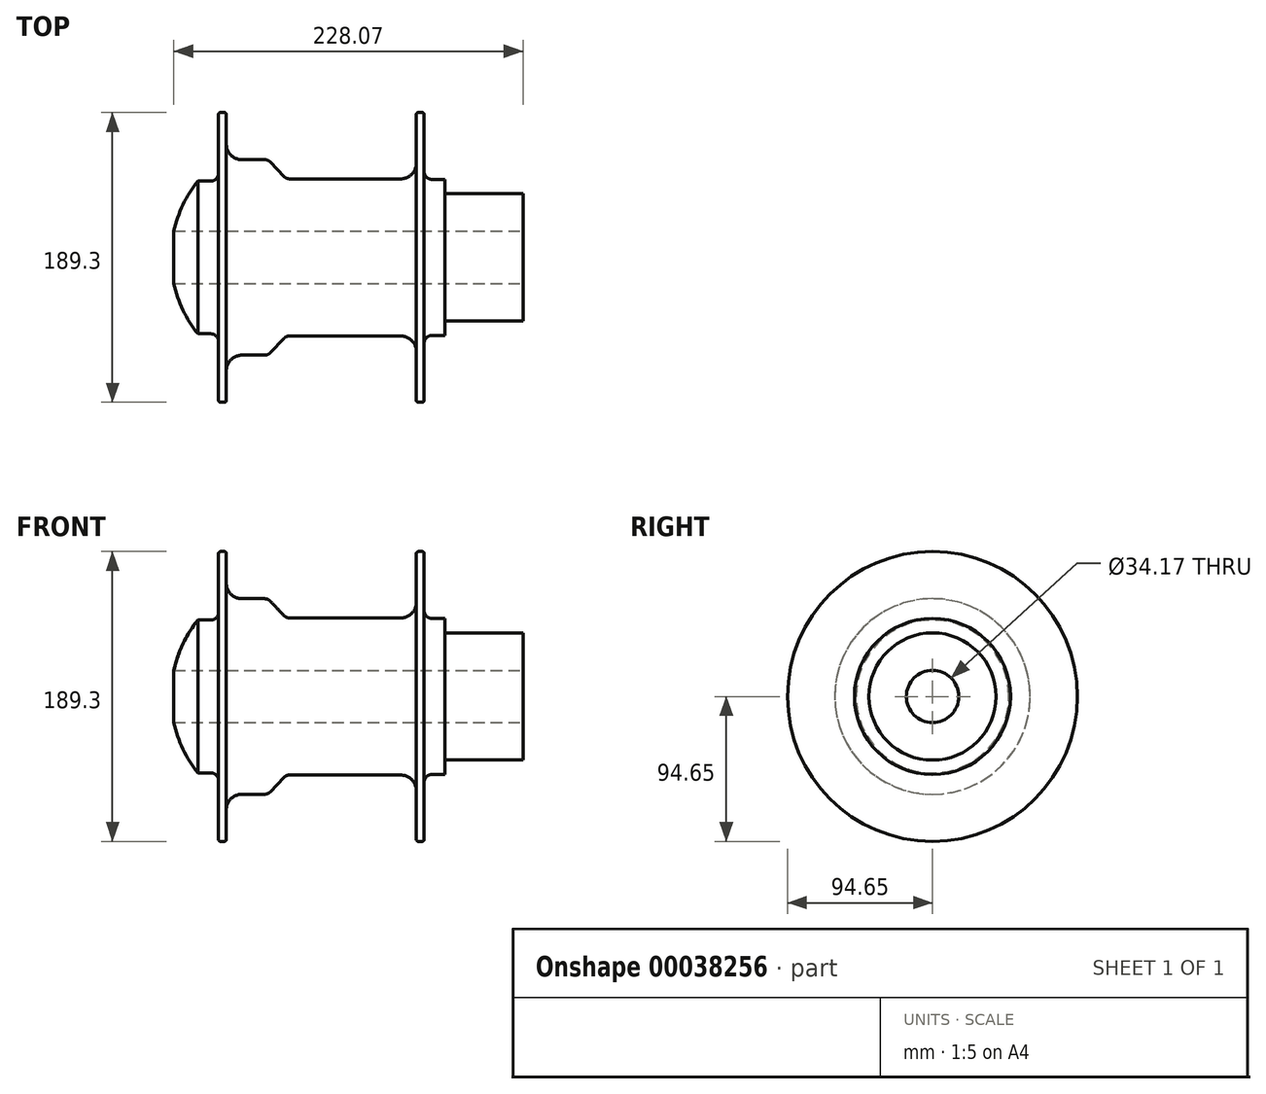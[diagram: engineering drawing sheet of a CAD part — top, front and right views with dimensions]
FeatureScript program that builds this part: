
annotation { "Feature Type Name" : "Feature", "Feature Type Description" : "" }
export const myFeature = defineFeature(function(context is Context, id is Id, definition is map)
    precondition{}
    {
        {
            var Q0;
            Q0=qCreatedBy(makeId("Front.planeOp"),FACE);
            var sketch = newSketch(context, id + "F0", { "sketchPlane" : qUnion([Q0])});
            skLineSegment(sketch, "E0", {"start": v(-97.3, 0) * mm, "end": v(100.15, 0) * mm, "construction": true});
            skLineSegment(sketch, "E1.bottom", {"start": v(-63.31, 0) * mm, "end": v(-55.52, 0) * mm});
            skLineSegment(sketch, "E1.top", {"start": v(-63.31, 49.9) * mm, "end": v(-55.52, 49.9) * mm});
            skLineSegment(sketch, "E1.left", {"start": v(-63.31, 0) * mm, "end": v(-63.31, 49.9) * mm});
            skLineSegment(sketch, "E1.right", {"start": v(-55.52, 0) * mm, "end": v(-55.52, 49.9) * mm});
            skLineSegment(sketch, "E2.bottom", {"start": v(-55.52, 0) * mm, "end": v(-50.44, 0) * mm});
            skLineSegment(sketch, "E2.top", {"start": v(-55.52, 94.65) * mm, "end": v(-50.44, 94.65) * mm});
            skLineSegment(sketch, "E2.left", {"start": v(-55.52, 0) * mm, "end": v(-55.52, 94.65) * mm});
            skLineSegment(sketch, "E2.right", {"start": v(-50.44, 0) * mm, "end": v(-50.44, 94.65) * mm});
            skLineSegment(sketch, "E3", {"start": v(-50.44, 63.85) * mm, "end": v(-23.18, 63.85) * mm});
            skLineSegment(sketch, "E4", {"start": v(-23.18, 63.85) * mm, "end": v(-11.37, 51.33) * mm});
            skLineSegment(sketch, "E5", {"start": v(-11.37, 51.33) * mm, "end": v(73.68, 51.33) * mm});
            skLineSegment(sketch, "E6.bottom", {"start": v(73.68, 0) * mm, "end": v(78.76, 0) * mm});
            skLineSegment(sketch, "E6.top", {"start": v(73.68, 94.65) * mm, "end": v(78.76, 94.65) * mm});
            skLineSegment(sketch, "E6.left", {"start": v(73.68, 0) * mm, "end": v(73.68, 94.65) * mm});
            skLineSegment(sketch, "E6.right", {"start": v(78.76, 0) * mm, "end": v(78.76, 94.65) * mm});
            skLineSegment(sketch, "E7.bottom", {"start": v(78.76, 0) * mm, "end": v(92.28, 0) * mm});
            skLineSegment(sketch, "E7.top", {"start": v(78.76, 50.97) * mm, "end": v(92.28, 50.97) * mm});
            skLineSegment(sketch, "E7.left", {"start": v(78.76, 0) * mm, "end": v(78.76, 50.97) * mm});
            skLineSegment(sketch, "E7.right", {"start": v(92.28, 0) * mm, "end": v(92.28, 50.97) * mm});
            skLineSegment(sketch, "E8", {"start": v(-50.44, 0) * mm, "end": v(73.68, 0) * mm});
            skLineSegment(sketch, "E9.bottom", {"start": v(-63.31, 0) * mm, "end": v(-69.08, 0) * mm});
            skLineSegment(sketch, "E9.top", {"start": v(-63.31, 49.9) * mm, "end": v(-69.08, 49.9) * mm});
            skLineSegment(sketch, "E9.right", {"start": v(-69.08, 0) * mm, "end": v(-69.08, 49.9) * mm});
            skArc(sketch, "E10", {"start": v(-69.08, 49.9) * mm, "mid": v(-82.04, 26.43) * mm, "end": v(-86.52, 0) * mm});
            skLineSegment(sketch, "E11", {"start": v(-69.08, 0) * mm, "end": v(-86.52, 0) * mm});
            skSolve(sketch);
        }
        {
            var Q0;
            Q0 = qSketchRegion(id + "F0", true);
            var Q1;
            Q1=sQuery(id+"F0.wireOp",EDGE,"E0");
            revolve(context, id + "F1", {"entities" : qUnion([Q0]), "axis" : qUnion([Q1]), "revolveType" : RevolveType.FULL});
        }
        {
            var Q0;
            Q0=makeQuery(id+"F1.opRevolve","SWEPT_EDGE",EDGE,{"disambiguationData":[OSD([sQuery(id+"F0.wireOp",EDGE,"E4"),sQuery(id+"F0.wireOp",EDGE,"E5")])]});
            var Q1;
            Q1=makeQuery(id+"F1.opRevolve","SWEPT_EDGE",EDGE,{"disambiguationData":[OSD([sQuery(id+"F0.wireOp",EDGE,"E3"),sQuery(id+"F0.wireOp",EDGE,"E4")])]});
            fillet(context, id + "F2", {"entities" : qUnion([Q0, Q1]), "radius" : 5.08 * mm, "tangentPropagation" : true, "allowEdgeOverflow" : false});
        }
        {
            var Q0;
            Q0=makeQuery(id+"F1.opRevolve","SWEPT_EDGE",EDGE,{"disambiguationData":[OSD([sQuery(id+"F0.wireOp",EDGE,"E2.right"),sQuery(id+"F0.wireOp",EDGE,"E3")])]});
            var Q1;
            Q1=makeQuery(id+"F1.opRevolve","SWEPT_EDGE",EDGE,{"disambiguationData":[OSD([sQuery(id+"F0.wireOp",EDGE,"E5"),sQuery(id+"F0.wireOp",EDGE,"E6.left")])]});
            fillet(context, id + "F3", {"entities" : qUnion([Q0, Q1]), "radius" : 10.16 * mm, "tangentPropagation" : true, "allowEdgeOverflow" : false});
        }
        {
            var Q0;
            Q0=makeQuery(id+"F1.opRevolve","SWEPT_FACE",FACE,{"disambiguationData":[OSD([sQuery(id+"F0.wireOp",EDGE,"E7.right")])]});
            var sketch = newSketch(context, id + "F4", { "sketchPlane" : qUnion([Q0])});
            skSolve(sketch);
        }
        {
            var Q0;
            Q0=makeQuery(id+"F1.opRevolve","SWEPT_EDGE",EDGE,{"disambiguationData":[OSD([sQuery(id+"F0.wireOp",EDGE,"E1.top"),sQuery(id+"F0.wireOp",EDGE,"E2.left")])]});
            var Q1;
            Q1=makeQuery(id+"F1.opRevolve","SWEPT_EDGE",EDGE,{"disambiguationData":[OSD([sQuery(id+"F0.wireOp",EDGE,"E6.right"),sQuery(id+"F0.wireOp",EDGE,"E7.top"),sQuery(id+"F0.wireOp",EDGE,"E7.left")])]});
            fillet(context, id + "F5", {"entities" : qUnion([Q0, Q1]), "radius" : 5.08 * mm, "tangentPropagation" : true, "allowEdgeOverflow" : false});
        }
        {
            var Q0;
            Q0=makeQuery(id+"F1.opRevolve","SWEPT_EDGE",EDGE,{"disambiguationData":[OSD([sQuery(id+"F0.wireOp",EDGE,"E2.top"),sQuery(id+"F0.wireOp",EDGE,"E2.right")])]});
            var Q1;
            Q1=makeQuery(id+"F1.opRevolve","SWEPT_EDGE",EDGE,{"disambiguationData":[OSD([sQuery(id+"F0.wireOp",EDGE,"E2.top"),sQuery(id+"F0.wireOp",EDGE,"E2.left")])]});
            var Q2;
            Q2=makeQuery(id+"F1.opRevolve","SWEPT_EDGE",EDGE,{"disambiguationData":[OSD([sQuery(id+"F0.wireOp",EDGE,"E6.top"),sQuery(id+"F0.wireOp",EDGE,"E6.right")])]});
            var Q3;
            Q3=makeQuery(id+"F1.opRevolve","SWEPT_EDGE",EDGE,{"disambiguationData":[OSD([sQuery(id+"F0.wireOp",EDGE,"E6.top"),sQuery(id+"F0.wireOp",EDGE,"E6.left")])]});
            fillet(context, id + "F6", {"entities" : qUnion([Q0, Q1, Q2, Q3]), "radius" : 1.27 * mm, "tangentPropagation" : true, "allowEdgeOverflow" : false});
        }
        {
            var Q0;
            Q0=makeQuery(id+"F4.imprint","IMPRINT",FACE,{"disambiguationData":[TD([[makeQuery(id+"F4.imprint","IMPRINT",EDGE,{"derivedFrom":makeQuery(id+"F1.opRevolve","SWEPT_EDGE",EDGE,{"disambiguationData":[OSD([sQuery(id+"F0.wireOp",EDGE,"E7.top"),sQuery(id+"F0.wireOp",EDGE,"E7.right")])]})}),-1.0]])]});
            var sketch = newSketch(context, id + "F7", { "sketchPlane" : qUnion([Q0])});
            skCircle(sketch, "E12", {"center": v(0, 0) * mm, "radius": 41.54 * mm});
            skSolve(sketch);
        }
        {
            var Q0;
            Q0=makeQuery(id+"F7.imprint","IMPRINT",FACE,{"disambiguationData":[TD([[makeQuery(id+"F7.imprint","IMPRINT",EDGE,{"derivedFrom":sQuery(id+"F7.wireOp",EDGE,"E12")}),1.0]])]});
            extrude(context, id + "F8", {"entities" : qUnion([Q0]), "operationType" : NewBodyOperationType.ADD, "depth" : 51.1 * mm});
        }
        {
            var Q0;
            Q0=makeQuery(id+"F8.opExtrude","CAP_FACE",FACE,{"disambiguationData":[OSD([sQuery(id+"F7.wireOp",EDGE,"E12")])],"isStart":false});
            var sketch = newSketch(context, id + "F9", { "sketchPlane" : qUnion([Q0])});
            skCircle(sketch, "E13", {"center": v(0, 0) * mm, "radius": 17.09 * mm});
            skSolve(sketch);
        }
        {
            var Q0;
            Q0 = qSketchRegion(id + "F9", true);
            extrude(context, id + "F10", {"entities" : qUnion([Q0]), "operationType" : NewBodyOperationType.REMOVE, "endBound" : BoundingType.THROUGH_ALL, "oppositeDirection" : true, "depth" : 25.4 * mm});
        }
    });
